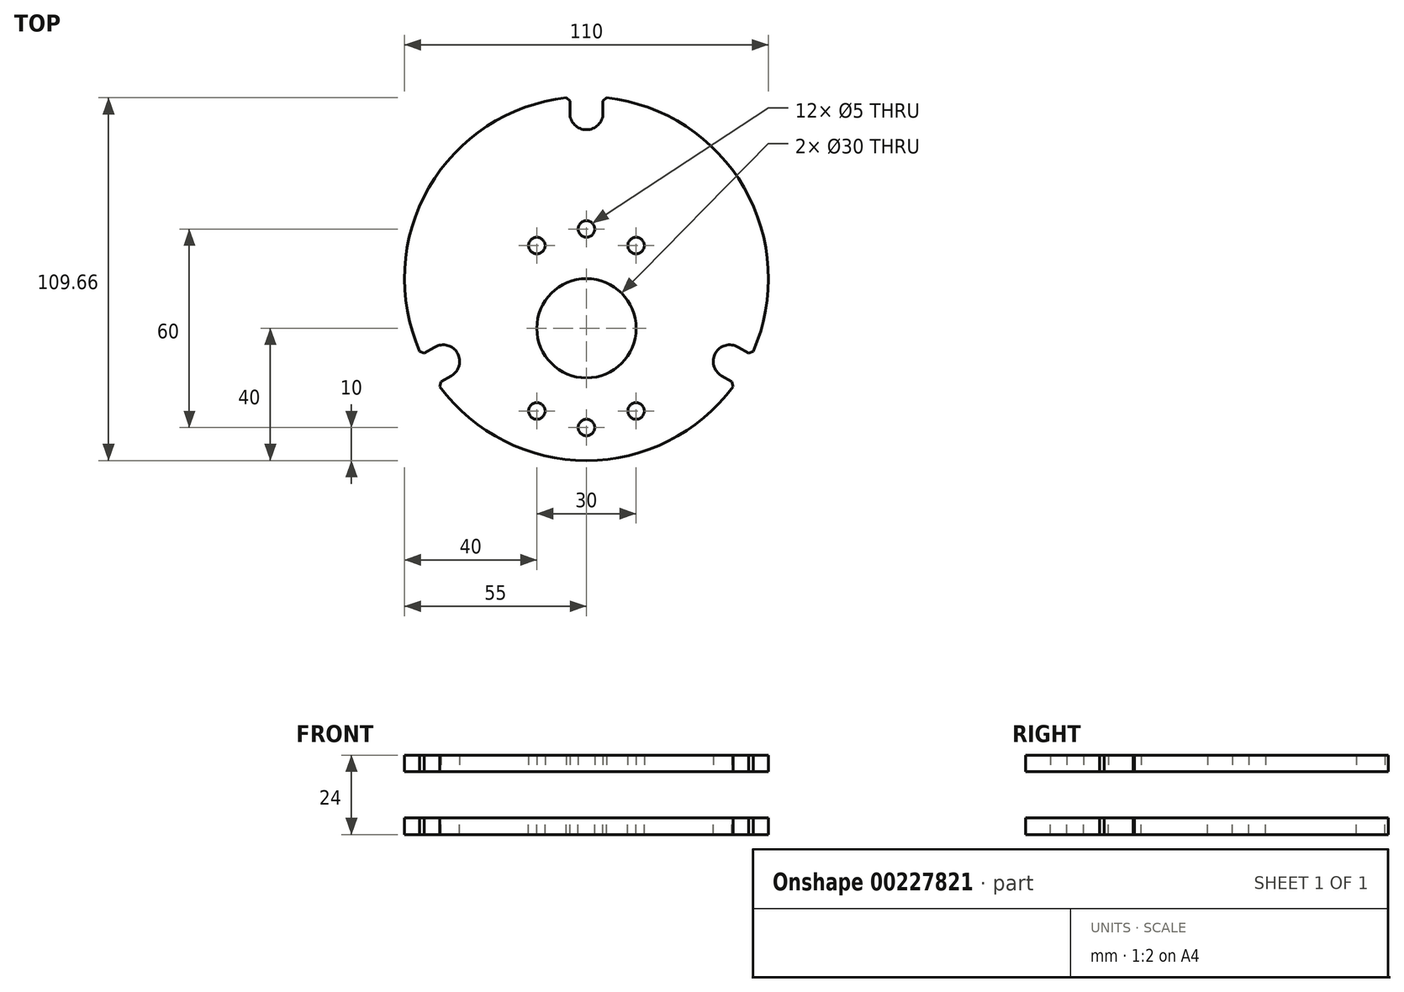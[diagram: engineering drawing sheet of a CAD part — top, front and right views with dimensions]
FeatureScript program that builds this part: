
annotation { "Feature Type Name" : "Feature", "Feature Type Description" : "" }
export const myFeature = defineFeature(function(context is Context, id is Id, definition is map)
    precondition{}
    {
        {
            var Q0;
            Q0=qCreatedBy(makeId("Top.planeOp"),FACE);
            var sketch = newSketch(context, id + "F0", { "sketchPlane" : qUnion([Q0])});
            skCircle(sketch, "E0", {"center": v(0, 0) * mm, "radius": 95 * mm, "construction": true});
            skPoint(sketch, "E1", {"position": v(0, -15) * mm});
            skPoint(sketch, "E2", {"position": v(0, 15) * mm});
            skCircle(sketch, "E3", {"center": v(0, 15) * mm, "radius": 80 * mm, "construction": true});
            skCircle(sketch, "E4", {"center": v(0, 15) * mm, "radius": 70 * mm, "construction": true});
            skLineSegment(sketch, "E5", {"start": v(0, 15) * mm, "end": v(-99.15, 72.25) * mm, "construction": true});
            skLineSegment(sketch, "E6.MirrorCS", {"start": v(0, 15) * mm, "end": v(99.15, 72.25) * mm, "construction": true});
            skArc(sketch, "E7.1.0", {"start": v(40.59, 44.2) * mm, "mid": v(7.54, 64.43) * mm, "end": v(-30.04, 54.97) * mm, "construction": true});
            skArc(sketch, "E8.trimOffspring", {"start": v(50.4, -7.04) * mm, "mid": v(47.63, 42.5) * mm, "end": v(6.11, 69.66) * mm});
            skArc(sketch, "E9.trimOffspring", {"start": v(-46.91, 32.3) * mm, "mid": v(1.75, -34.97) * mm, "end": v(45.58, 35.55) * mm, "construction": true});
            skCircle(sketch, "E10", {"center": v(0, 0) * mm, "radius": 15 * mm});
            skArc(sketch, "E11", {"start": v(-5, 65) * mm, "mid": v(0, 60) * mm, "end": v(5, 65) * mm});
            skLineSegment(sketch, "E12", {"start": v(5, 68.67) * mm, "end": v(5, 64.75) * mm});
            skLineSegment(sketch, "E13", {"start": v(-5, 68.67) * mm, "end": v(-5, 64.75) * mm});
            skArc(sketch, "E14.trimOffspring", {"start": v(-6.11, 69.66) * mm, "mid": v(-47.36, 42.97) * mm, "end": v(-50.82, -6.03) * mm});
            skLineSegment(sketch, "E15", {"start": v(-6.11, 69.66) * mm, "end": v(-5, 68.67) * mm});
            skLineSegment(sketch, "E16", {"start": v(6.11, 69.66) * mm, "end": v(5, 68.67) * mm});
            skCircle(sketch, "E17", {"center": v(0, 65) * mm, "radius": 5 * mm, "construction": true});
            skCircle(sketch, "E18", {"center": v(0, 65) * mm, "radius": 8.5 * mm, "construction": true});
            skCircle(sketch, "E19", {"center": v(0, 65) * mm, "radius": 20 * mm, "construction": true});
            skCircle(sketch, "E20.1.0", {"center": v(-43.3, -10) * mm, "radius": 8.5 * mm, "construction": true});
            skPoint(sketch, "E20.1.1", {"position": v(-43.3, -10) * mm});
            skCircle(sketch, "E20.1.2", {"center": v(-43.3, -10) * mm, "radius": 5 * mm, "construction": true});
            skLineSegment(sketch, "E20.1.3", {"start": v(-43.98, -16.16) * mm, "end": v(-40.58, -14.2) * mm});
            skArc(sketch, "E20.1.4", {"start": v(-40.8, -14.33) * mm, "mid": v(-38.97, -7.5) * mm, "end": v(-45.8, -5.67) * mm});
            skLineSegment(sketch, "E20.1.5", {"start": v(-44.28, -17.62) * mm, "end": v(-43.98, -16.16) * mm});
            skLineSegment(sketch, "E20.1.6", {"start": v(-48.98, -7.5) * mm, "end": v(-45.58, -5.54) * mm});
            skLineSegment(sketch, "E20.1.7", {"start": v(-50.4, -7.04) * mm, "end": v(-48.98, -7.5) * mm});
            skCircle(sketch, "E20.1.8", {"center": v(-43.3, -10) * mm, "radius": 20 * mm, "construction": true});
            skCircle(sketch, "E20.2.0", {"center": v(43.3, -10) * mm, "radius": 8.5 * mm, "construction": true});
            skPoint(sketch, "E20.2.1", {"position": v(43.3, -10) * mm});
            skCircle(sketch, "E20.2.2", {"center": v(43.3, -10) * mm, "radius": 5 * mm, "construction": true});
            skLineSegment(sketch, "E20.2.3", {"start": v(48.98, -7.5) * mm, "end": v(45.58, -5.54) * mm});
            skArc(sketch, "E20.2.4", {"start": v(45.8, -5.67) * mm, "mid": v(38.97, -7.5) * mm, "end": v(40.8, -14.33) * mm});
            skLineSegment(sketch, "E20.2.5", {"start": v(50.4, -7.04) * mm, "end": v(48.98, -7.5) * mm});
            skLineSegment(sketch, "E20.2.6", {"start": v(43.98, -16.16) * mm, "end": v(40.58, -14.2) * mm});
            skLineSegment(sketch, "E20.2.7", {"start": v(44.28, -17.62) * mm, "end": v(43.98, -16.16) * mm});
            skCircle(sketch, "E20.2.8", {"center": v(43.3, -10) * mm, "radius": 20 * mm, "construction": true});
            skArc(sketch, "E21.trimOffspring", {"start": v(-50.82, -6.03) * mm, "mid": v(-50.6, -6.54) * mm, "end": v(-50.4, -7.04) * mm});
            skArc(sketch, "E22.trimOffspring", {"start": v(-44.28, -17.62) * mm, "mid": v(0, -40) * mm, "end": v(44.28, -17.62) * mm});
            skCircle(sketch, "E23", {"center": v(0, 0) * mm, "radius": 55 * mm, "construction": true});
            skCircle(sketch, "E24", {"center": v(0, 0) * mm, "radius": 40 * mm, "construction": true});
            skCircle(sketch, "E25", {"center": v(0, 0) * mm, "radius": 33.5 * mm, "construction": true});
            skLineSegment(sketch, "E26", {"start": v(-15, 12.1) * mm, "end": v(-15, -37.02) * mm, "construction": true});
            skLineSegment(sketch, "E27", {"start": v(-31.23, -25) * mm, "end": v(-2.5, -25) * mm, "construction": true});
            skLineSegment(sketch, "E28", {"start": v(-31.23, -30) * mm, "end": v(8.76, -30) * mm, "construction": true});
            skCircle(sketch, "E29", {"center": v(-15, -25) * mm, "radius": 2.5 * mm});
            skCircle(sketch, "E30", {"center": v(0, -30) * mm, "radius": 2.5 * mm});
            skCircle(sketch, "E31.MirrorC", {"center": v(15, -25) * mm, "radius": 2.5 * mm});
            skCircle(sketch, "E32.MirrorC", {"center": v(-15, 25) * mm, "radius": 2.5 * mm});
            skCircle(sketch, "E33.MirrorC", {"center": v(15, 25) * mm, "radius": 2.5 * mm});
            skCircle(sketch, "E34.MirrorC", {"center": v(0, 30) * mm, "radius": 2.5 * mm});
            skSolve(sketch);
        }
        {
            var Q0;
            Q0 = qSketchRegion(id + "F0", true);
            extrude(context, id + "F1", {"entities" : qUnion([Q0]), "depth" : 12 * mm, "hasSecondDirection" : true, "secondDirectionOppositeDirection" : false, "secondDirectionDepth" : 7 * mm});
        }
        {
            var Q0;
            Q0 = qSketchRegion(id + "F0", true);
            extrude(context, id + "F2", {"entities" : qUnion([Q0]), "operationType" : NewBodyOperationType.ADD, "oppositeDirection" : true, "depth" : 12 * mm, "hasSecondDirection" : true, "secondDirectionOppositeDirection" : true, "secondDirectionDepth" : 7 * mm});
        }
    });
